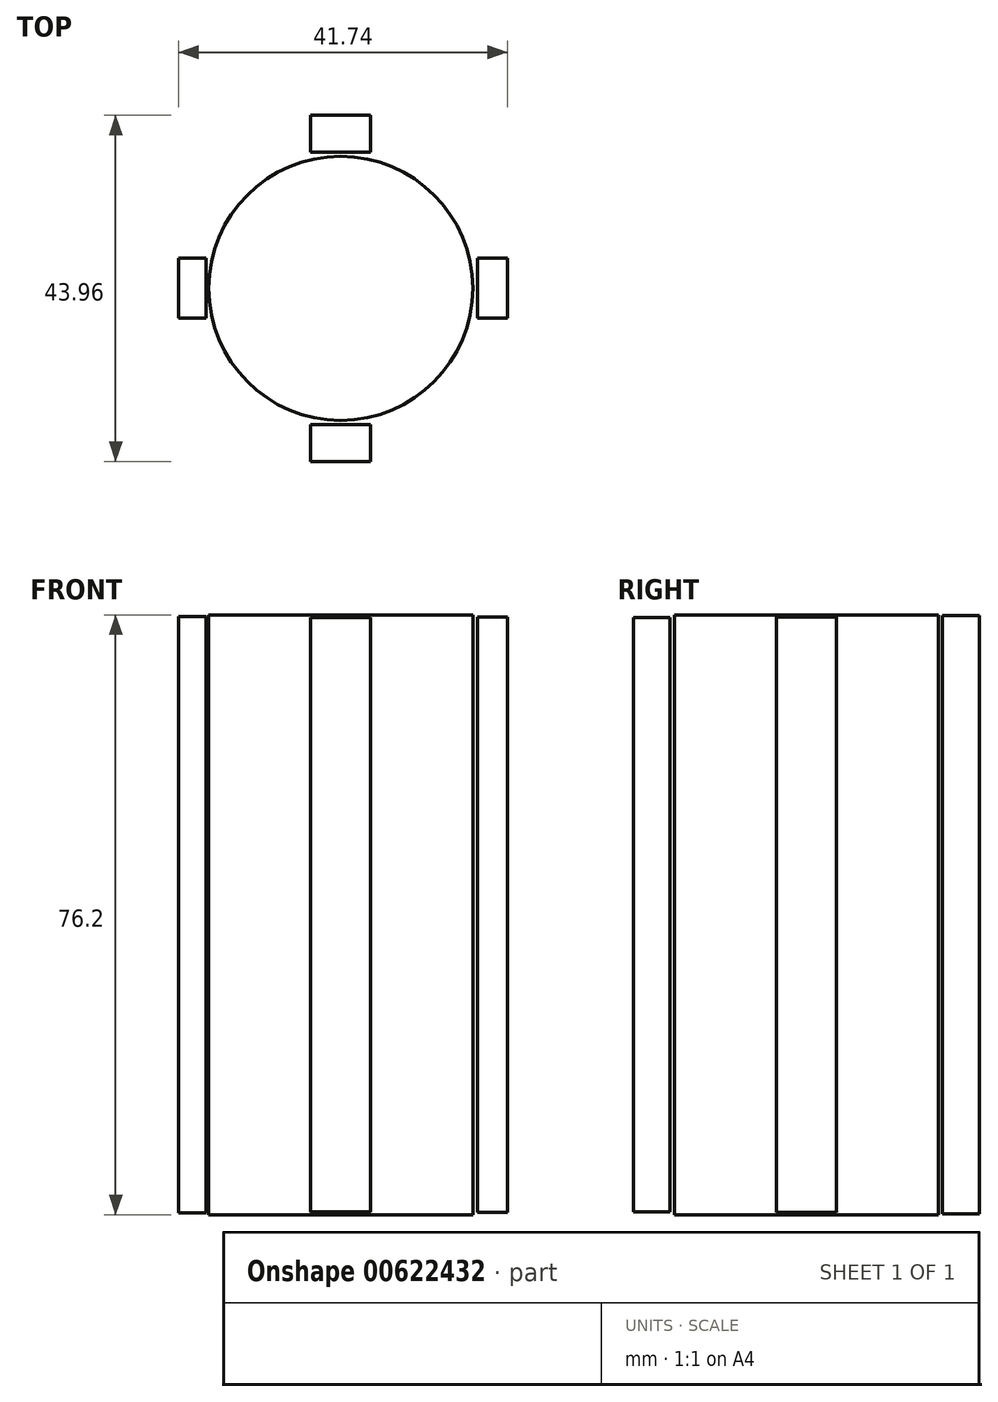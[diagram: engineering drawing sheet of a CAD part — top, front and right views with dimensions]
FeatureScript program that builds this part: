
annotation { "Feature Type Name" : "Feature", "Feature Type Description" : "" }
export const myFeature = defineFeature(function(context is Context, id is Id, definition is map)
    precondition{}
    {
        {
            var Q0;
            Q0=qCreatedBy(makeId("Top.planeOp"),FACE);
            var sketch = newSketch(context, id + "F0", { "sketchPlane" : qUnion([Q0])});
            skCircle(sketch, "E0", {"center": v(0, 0) * mm, "radius": 16.77 * mm});
            skSolve(sketch);
        }
        {
            var Q0;
            Q0 = qSketchRegion(id + "F0", true);
            extrude(context, id + "F1", {"entities" : qUnion([Q0]), "oppositeDirection" : true, "depth" : 38.1 * mm, "offsetDistance" : 25.4 * mm, "hasSecondDirection" : true, "secondDirectionOppositeDirection" : false, "secondDirectionDepth" : 38.1 * mm});
        }
        {
            var Q0;
            Q0=qCreatedBy(makeId("Right.planeOp"),FACE);
            var sketch = newSketch(context, id + "F2", { "sketchPlane" : qUnion([Q0])});
            skLineSegment(sketch, "E1.bottom", {"start": v(-21.98, -37.74) * mm, "end": v(-17.31, -37.74) * mm});
            skLineSegment(sketch, "E1.top", {"start": v(-21.98, 37.74) * mm, "end": v(-17.31, 37.74) * mm});
            skLineSegment(sketch, "E1.left", {"start": v(-21.98, -37.74) * mm, "end": v(-21.98, 37.74) * mm});
            skLineSegment(sketch, "E1.right", {"start": v(-17.31, -37.74) * mm, "end": v(-17.31, 37.74) * mm});
            skPoint(sketch, "E1.middle", {"position": v(-19.65, 0) * mm});
            skSolve(sketch);
        }
        {
            var Q0;
            Q0 = qSketchRegion(id + "F2", true);
            extrude(context, id + "F3", {"entities" : qUnion([Q0]), "depth" : 3.8 * mm, "offsetDistance" : 25.4 * mm, "hasSecondDirection" : true, "secondDirectionOppositeDirection" : true, "secondDirectionDepth" : 3.8 * mm});
        }
        {
            var Q0;
            Q0=qCreatedBy(makeId("Right.planeOp"),FACE);
            var sketch = newSketch(context, id + "F4", { "sketchPlane" : qUnion([Q0])});
            skLineSegment(sketch, "E2.bottom", {"start": v(17.28, -38) * mm, "end": v(21.98, -38) * mm});
            skLineSegment(sketch, "E2.top", {"start": v(17.28, 38) * mm, "end": v(21.98, 38) * mm});
            skLineSegment(sketch, "E2.left", {"start": v(17.28, -38) * mm, "end": v(17.28, 38) * mm});
            skLineSegment(sketch, "E2.right", {"start": v(21.98, -38) * mm, "end": v(21.98, 38) * mm});
            skPoint(sketch, "E2.middle", {"position": v(19.63, 0) * mm});
            skSolve(sketch);
        }
        {
            var Q0;
            Q0 = qSketchRegion(id + "F4", true);
            extrude(context, id + "F5", {"entities" : qUnion([Q0]), "oppositeDirection" : true, "depth" : 3.8 * mm, "offsetDistance" : 25.4 * mm, "hasSecondDirection" : true, "secondDirectionOppositeDirection" : false, "secondDirectionDepth" : 3.8 * mm});
        }
        {
            var Q0;
            Q0=qCreatedBy(makeId("Front.planeOp"),FACE);
            var sketch = newSketch(context, id + "F6", { "sketchPlane" : qUnion([Q0])});
            skLineSegment(sketch, "E3.bottom", {"start": v(21.17, -37.8) * mm, "end": v(17.39, -37.8) * mm});
            skLineSegment(sketch, "E3.top", {"start": v(21.17, 37.8) * mm, "end": v(17.39, 37.8) * mm});
            skLineSegment(sketch, "E3.left", {"start": v(21.17, -37.8) * mm, "end": v(21.17, 37.8) * mm});
            skLineSegment(sketch, "E3.right", {"start": v(17.39, -37.8) * mm, "end": v(17.39, 37.8) * mm});
            skPoint(sketch, "E3.middle", {"position": v(19.28, 0) * mm});
            skSolve(sketch);
        }
        {
            var Q0;
            Q0 = qSketchRegion(id + "F6", true);
            extrude(context, id + "F7", {"entities" : qUnion([Q0]), "oppositeDirection" : true, "depth" : 3.8 * mm, "offsetDistance" : 25.4 * mm, "hasSecondDirection" : true, "secondDirectionOppositeDirection" : false, "secondDirectionDepth" : 3.8 * mm});
        }
        {
            var Q0;
            Q0=qCreatedBy(makeId("Front.planeOp"),FACE);
            var sketch = newSketch(context, id + "F8", { "sketchPlane" : qUnion([Q0])});
            skLineSegment(sketch, "E4.bottom", {"start": v(-20.57, 37.87) * mm, "end": v(-17.08, 37.87) * mm});
            skLineSegment(sketch, "E4.top", {"start": v(-20.57, -37.87) * mm, "end": v(-17.08, -37.87) * mm});
            skLineSegment(sketch, "E4.left", {"start": v(-20.57, 37.87) * mm, "end": v(-20.57, -37.87) * mm});
            skLineSegment(sketch, "E4.right", {"start": v(-17.08, 37.87) * mm, "end": v(-17.08, -37.87) * mm});
            skPoint(sketch, "E4.middle", {"position": v(-18.83, 0) * mm});
            skSolve(sketch);
        }
        {
            var Q0;
            Q0 = qSketchRegion(id + "F8", true);
            extrude(context, id + "F9", {"entities" : qUnion([Q0]), "oppositeDirection" : true, "depth" : 3.8 * mm, "offsetDistance" : 25.4 * mm, "hasSecondDirection" : true, "secondDirectionOppositeDirection" : false, "secondDirectionDepth" : 3.8 * mm});
        }
    });
